# Revit family: 0060582 Sylvania Lighting Fixture START Spot Scoop 1800lm 930 MB WHT
name_source: partatom
category: Lighting Fixtures
revit_build: Autodesk Revit 2016 (Build: 20150220_1215(x64)
units: mm (PartAtom-declared; Revit-internal decimal feet)

## family parameters
Cut with Voids When Loaded = No
Host = Face
Light Source = No
OmniClass Number = 23.80.70.00
OmniClass Title = Lighting
Part Type = Normal
Room Calculation Point = No
Round Connector Dimension = Use Diameter
Shared = No

## types (1)
- 0060582 START Spot Scoop 1800lm 930 MB WHT
    Apparent Load = 20 VA
    Assembly Code = D5020200
    AssetType = Fixed
    ClassificationName = Uniclass2015
    ClassificationValue = EF_70_80
    Cost = 0 $
    Default Elevation = 1219 mm
    Description = Recessed Adjustable Accent Downlight, integrated LED, die cast aluminium body, Ø155mm cut-out, CCT 3000K, 1800lm, total power consumption 20W, resulting in 90lm/W.
    DimmingControlOptions = Non dimmable
    DocumentationLiterature = http://www.sylvania-lighting.com
    DurationUnit = hours
    ElectricShockClassification = Class II
    ExpectedLife = 50000
    IfcExportAs = IfcLightFixtureType
    IfcExportType = IfcLightFixtureType
    ImpactProtectionIndex = IK03
    IngressProtection = IP40
    Keynote = 16500
    Lamp = LED
    LampColourRenderingIndex = 90
    LampColourTemperature = 3000 K
    LampNominalLuminous = 1800  lm
    LampsType = LED
    LuminousEfficacy = 90 lm/W
    M_SYL = Yes
    Manufacturer = Feilo Sylvania
    ManufacturerName = Feilo Sylvania
    Material_1_SYL = PC/ABS Plastic
    Model = START Spot Scoop 1800lm 930 MB WHT
    ModelNumber = 0060582
    ModelReference = START Spot Scoop 1800lm 930 MB WHT
    Name = START Spot Scoop 1800lm 930 MB WHT
    NominalDepth = 167 mm
    NominalHeight = 145 mm
    NominalLength = 167 mm
    PowerConsumption = 20 W
    PowerFactor = 0
    Rad1_SYL = 84 mm
    Rad2_SYL = 78 mm
    Rad3_SYL = 74 mm
    Rad4_SYL = 68 mm
    S_SYL = No
    Type Image = <None>
    TypeHeadM_SYL = START Spot Scoop Head M : 0060582 START Spot Scoop 1800lm 930 MB WHT
    TypeName = START Spot Scoop 1800lm 930 MB WHT
    URL = http://www.sylvania-lighting.com
    Voltage = 230 V
    Weight = 11.752 kg

## geometry (parser evidence)
native form markers: Sweep x5
no freeform markers — native parametric forms only
